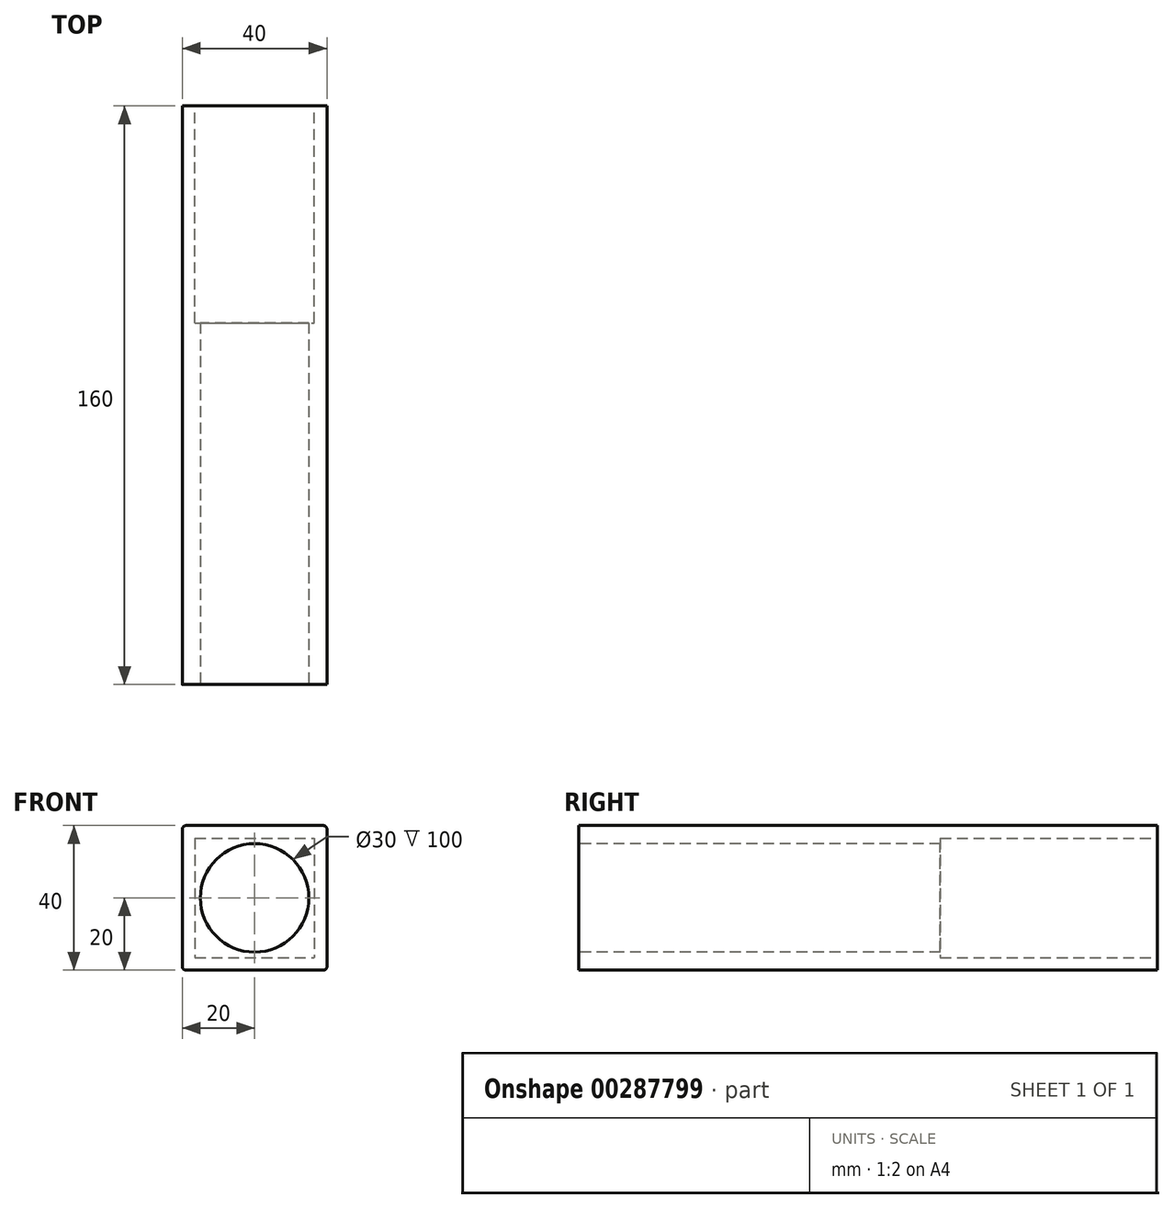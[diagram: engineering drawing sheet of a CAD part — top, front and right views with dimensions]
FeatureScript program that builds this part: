
annotation { "Feature Type Name" : "Feature", "Feature Type Description" : "" }
export const myFeature = defineFeature(function(context is Context, id is Id, definition is map)
    precondition{}
    {
        {
            var Q0;
            Q0=qCreatedBy(makeId("Front.planeOp"),FACE);
            var sketch = newSketch(context, id + "F0", { "sketchPlane" : qUnion([Q0])});
            skLineSegment(sketch, "E0.bottom", {"start": v(20, 20) * mm, "end": v(-20, 20) * mm});
            skLineSegment(sketch, "E0.top", {"start": v(20, -20) * mm, "end": v(-20, -20) * mm});
            skLineSegment(sketch, "E0.left", {"start": v(20, 20) * mm, "end": v(20, -20) * mm});
            skLineSegment(sketch, "E0.right", {"start": v(-20, 20) * mm, "end": v(-20, -20) * mm});
            skPoint(sketch, "E0.middle", {"position": v(0, 0) * mm});
            skSolve(sketch);
        }
        {
            var Q0;
            Q0=makeQuery(id+"F0.imprint","IMPRINT",FACE,{"disambiguationData":[TD([[makeQuery(id+"F0.imprint","IMPRINT",EDGE,{"derivedFrom":sQuery(id+"F0.wireOp",EDGE,"E0.bottom")}),1.0]])]});
            extrude(context, id + "F1", {"entities" : qUnion([Q0]), "depth" : 160 * mm});
        }
        {
            var Q0;
            Q0=makeQuery(id+"F1.opExtrude","CAP_FACE",FACE,{"disambiguationData":[OSD([sQuery(id+"F0.wireOp",EDGE,"E0.bottom"),sQuery(id+"F0.wireOp",EDGE,"E0.top"),sQuery(id+"F0.wireOp",EDGE,"E0.left"),sQuery(id+"F0.wireOp",EDGE,"E0.right")])],"isStart":false});
            var sketch = newSketch(context, id + "F2", { "sketchPlane" : qUnion([Q0])});
            skCircle(sketch, "E1", {"center": v(0, 0) * mm, "radius": 15 * mm});
            skSolve(sketch);
        }
        {
            var Q0;
            Q0=makeQuery(id+"F2.imprint","IMPRINT",FACE,{"disambiguationData":[TD([[makeQuery(id+"F2.imprint","IMPRINT",EDGE,{"derivedFrom":sQuery(id+"F2.wireOp",EDGE,"E1")}),1.0]])]});
            extrude(context, id + "F3", {"entities" : qUnion([Q0]), "operationType" : NewBodyOperationType.REMOVE, "oppositeDirection" : true, "depth" : 100 * mm});
        }
        {
            var Q0;
            Q0=makeQuery(id+"F1.opExtrude","CAP_FACE",FACE,{"disambiguationData":[OSD([sQuery(id+"F0.wireOp",EDGE,"E0.bottom"),sQuery(id+"F0.wireOp",EDGE,"E0.top"),sQuery(id+"F0.wireOp",EDGE,"E0.left"),sQuery(id+"F0.wireOp",EDGE,"E0.right")])],"isStart":true});
            var sketch = newSketch(context, id + "F4", { "sketchPlane" : qUnion([Q0])});
            skLineSegment(sketch, "E2.bottom", {"start": v(16.5, 16.5) * mm, "end": v(-16.5, 16.5) * mm});
            skLineSegment(sketch, "E2.top", {"start": v(16.5, -16.5) * mm, "end": v(-16.5, -16.5) * mm});
            skLineSegment(sketch, "E2.left", {"start": v(16.5, 16.5) * mm, "end": v(16.5, -16.5) * mm});
            skLineSegment(sketch, "E2.right", {"start": v(-16.5, 16.5) * mm, "end": v(-16.5, -16.5) * mm});
            skPoint(sketch, "E2.middle", {"position": v(0, 0) * mm});
            skSolve(sketch);
        }
        {
            var Q0;
            Q0=makeQuery(id+"F4.imprint","IMPRINT",FACE,{"disambiguationData":[TD([[makeQuery(id+"F4.imprint","IMPRINT",EDGE,{"derivedFrom":sQuery(id+"F4.wireOp",EDGE,"E2.bottom")}),1.0]])]});
            extrude(context, id + "F5", {"entities" : qUnion([Q0]), "operationType" : NewBodyOperationType.REMOVE, "oppositeDirection" : true, "depth" : 60 * mm});
        }
        {
            var Q0;
            Q0=makeQuery(id+"F1.opExtrude","SWEPT_EDGE",EDGE,{"disambiguationData":[OSD([sQuery(id+"F0.wireOp",EDGE,"E0.bottom"),sQuery(id+"F0.wireOp",EDGE,"E0.left")])]});
            var Q1;
            Q1=makeQuery(id+"F1.opExtrude","SWEPT_EDGE",EDGE,{"disambiguationData":[OSD([sQuery(id+"F0.wireOp",EDGE,"E0.bottom"),sQuery(id+"F0.wireOp",EDGE,"E0.right")])]});
            var Q2;
            Q2=makeQuery(id+"F1.opExtrude","SWEPT_EDGE",EDGE,{"disambiguationData":[OSD([sQuery(id+"F0.wireOp",EDGE,"E0.top"),sQuery(id+"F0.wireOp",EDGE,"E0.left")])]});
            var Q3;
            Q3=makeQuery(id+"F1.opExtrude","SWEPT_EDGE",EDGE,{"disambiguationData":[OSD([sQuery(id+"F0.wireOp",EDGE,"E0.top"),sQuery(id+"F0.wireOp",EDGE,"E0.right")])]});
            fillet(context, id + "F6", {"entities" : qUnion([Q0, Q1, Q2, Q3]), "radius" : 1 * mm, "tangentPropagation" : true, "allowEdgeOverflow" : false});
        }
    });
